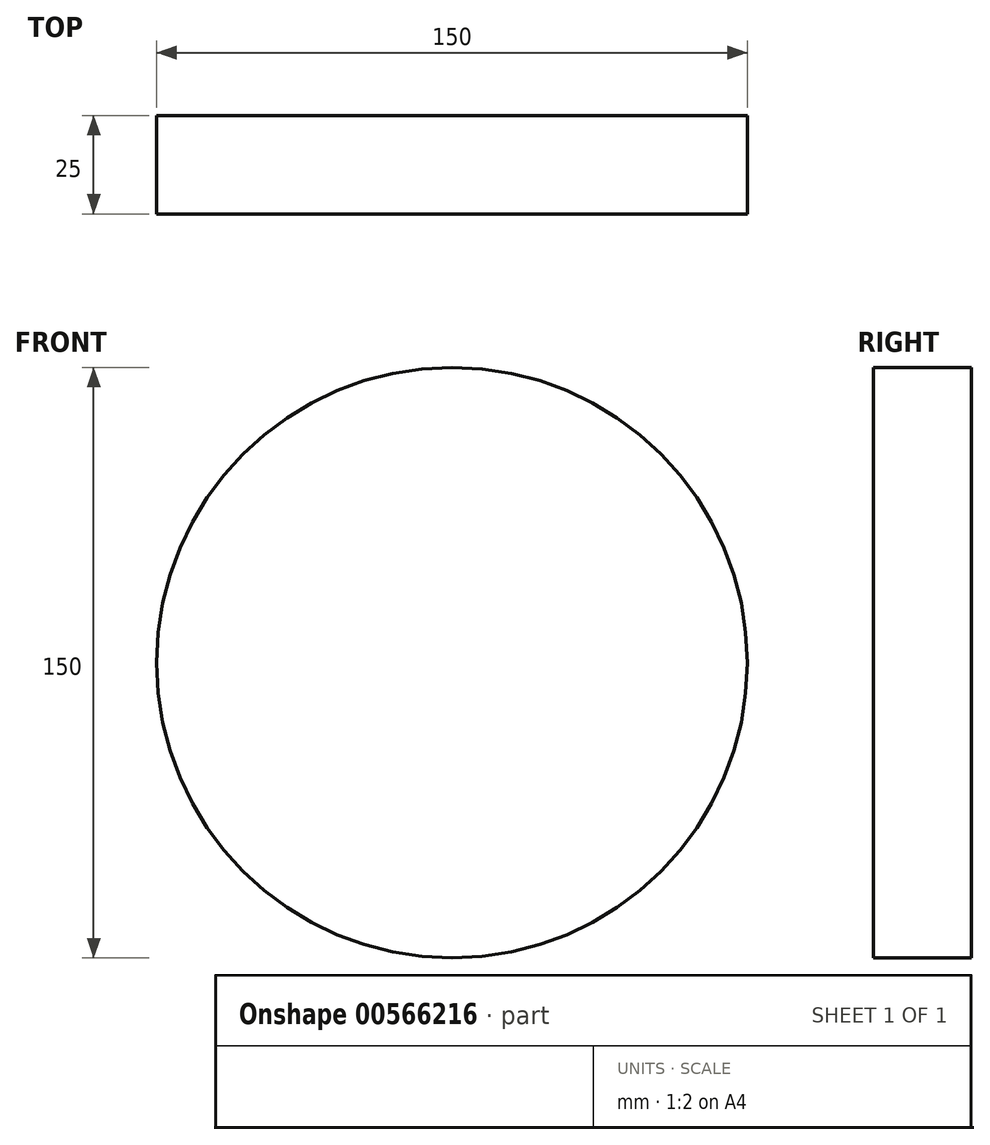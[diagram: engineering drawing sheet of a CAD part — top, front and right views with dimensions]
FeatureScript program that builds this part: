
annotation { "Feature Type Name" : "Feature", "Feature Type Description" : "" }
export const myFeature = defineFeature(function(context is Context, id is Id, definition is map)
    precondition{}
    {
        {
            var Q0;
            Q0=qCreatedBy(makeId("Front.planeOp"),FACE);
            var sketch = newSketch(context, id + "F0", { "sketchPlane" : qUnion([Q0])});
            skCircle(sketch, "E0", {"center": v(0, 0) * mm, "radius": 75 * mm});
            skSolve(sketch);
        }
        {
            var Q0;
            Q0=makeQuery(id+"F0.imprint","IMPRINT",FACE,{"disambiguationData":[TD([[makeQuery(id+"F0.imprint","IMPRINT",EDGE,{"derivedFrom":sQuery(id+"F0.wireOp",EDGE,"E0")}),1.0]])]});
            extrude(context, id + "F1", {"entities" : qUnion([Q0]), "endBound" : BoundingType.SYMMETRIC, "depth" : 25 * mm, "offsetDistance" : 25 * mm});
        }
    });
